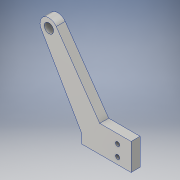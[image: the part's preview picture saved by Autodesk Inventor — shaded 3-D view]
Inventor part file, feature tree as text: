
AUTODESK INVENTOR PART (.ipt)
format: ipt  version: 2016 (Build 200138000, 138)  size: 124,928 bytes
history: native  units: in
note: dims shown in document units (in); Inventor stores cm internally (conversion verified against a paired STEP export)
features: thread x2, extrude x1, sketch x1
ambient origin geometry x8: Origin, YZ Plane, XZ Plane, XY Plane, X Axis, Y Axis, Z Axis, Center Point
bodies: Solid1 (feature_tree)
feature tree (4):
  extrude  "Extrusion1"  Depth=0.75in
  thread  "Thread1"  [1 undecoded]
  thread  "Thread2"  [1 undecoded]
  sketch  "Sketch1"  dims[d0=1.375in d1=0.75in d2=0.26in d3=150.0deg d4=1.59in d13=0.25in d14=0.0in d16=1.0in d17=0.25in d18=0.3125in d19=1.0in d20=0.1181in d21=0.1181in d22=0.5in d23=0.5in d24=0.5in d25=1.0in d26=0.0in d27=1.0in d28=0.0in]
note: 2 required parameter values undecoded (feature->parameter linkage not recoverable at this tier; creation-order binding heuristic only, values carry confidence <= 0.55)
